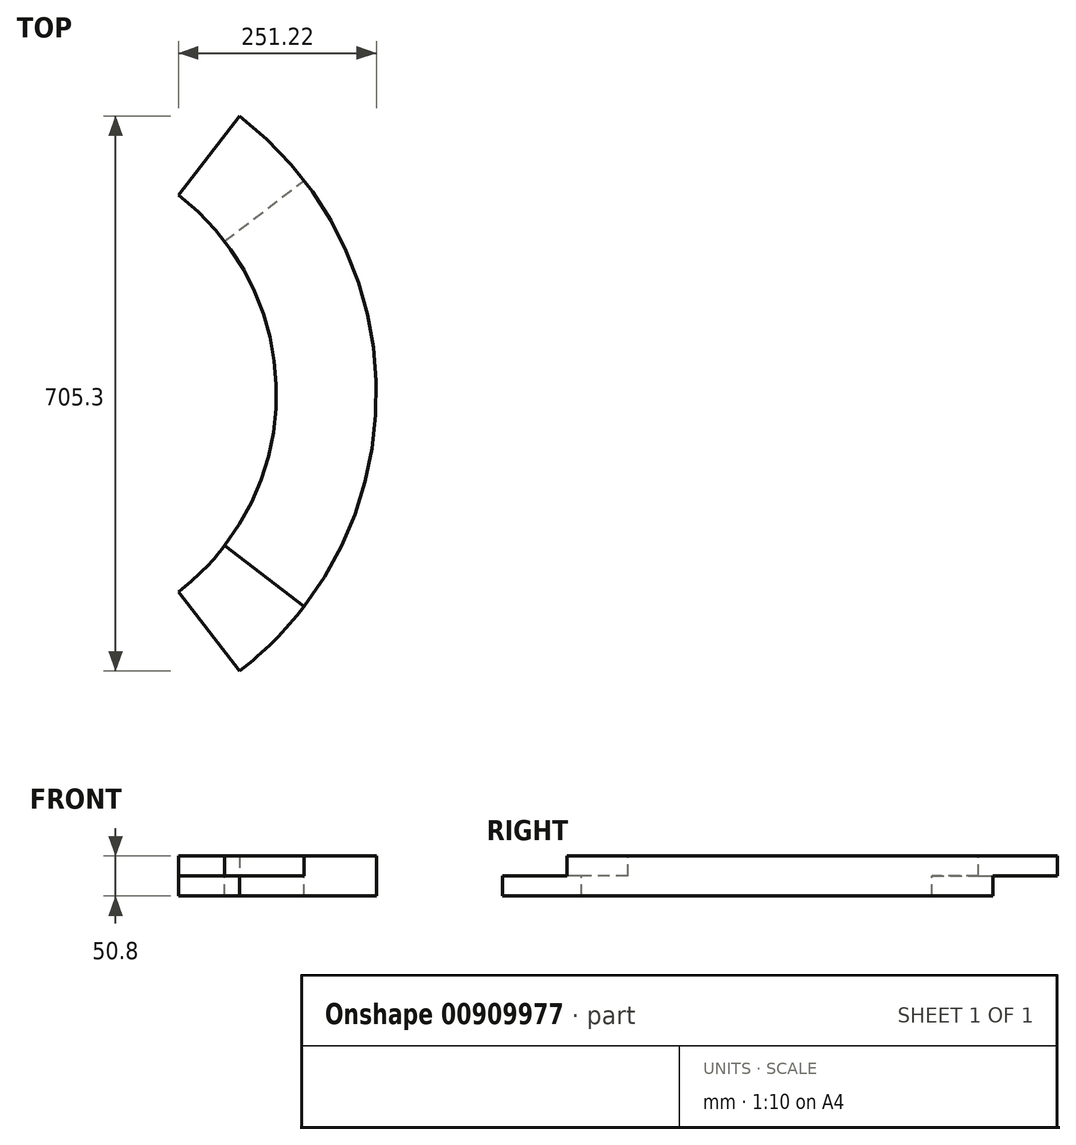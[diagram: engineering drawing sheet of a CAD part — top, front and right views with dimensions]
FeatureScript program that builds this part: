
annotation { "Feature Type Name" : "Feature", "Feature Type Description" : "" }
export const myFeature = defineFeature(function(context is Context, id is Id, definition is map)
    precondition{}
    {
        {
            var Q0;
            Q0=qCreatedBy(makeId("Front.planeOp"),FACE);
            var sketch = newSketch(context, id + "F0", { "sketchPlane" : qUnion([Q0])});
            skLineSegment(sketch, "E0.bottom", {"start": v(317.5, 0) * mm, "end": v(444.5, 0) * mm});
            skLineSegment(sketch, "E0.top", {"start": v(317.5, 25.4) * mm, "end": v(444.5, 25.4) * mm});
            skLineSegment(sketch, "E0.left", {"start": v(317.5, 0) * mm, "end": v(317.5, 25.4) * mm});
            skLineSegment(sketch, "E0.right", {"start": v(444.5, 0) * mm, "end": v(444.5, 25.4) * mm});
            skLineSegment(sketch, "E1", {"start": v(317.5, 25.4) * mm, "end": v(317.5, 50.8) * mm});
            skLineSegment(sketch, "E2", {"start": v(317.5, 50.8) * mm, "end": v(444.5, 50.8) * mm});
            skLineSegment(sketch, "E3", {"start": v(444.5, 50.8) * mm, "end": v(444.5, 25.4) * mm});
            skLineSegment(sketch, "E4", {"start": v(0, 0) * mm, "end": v(0, 51.24) * mm, "construction": true});
            skSolve(sketch);
        }
        {
            var Q0;
            Q0=makeQuery(id+"F0.imprint","IMPRINT",FACE,{"disambiguationData":[TD([[makeQuery(id+"F0.imprint","IMPRINT",EDGE,{"derivedFrom":sQuery(id+"F0.wireOp",EDGE,"E0.bottom")}),1.0]])]});
            var Q1;
            Q1=sQuery(id+"F0.wireOp",EDGE,"E4");
            revolve(context, id + "F1", {"surfaceOperationType" : NewSurfaceOperationType.NEW, "entities" : qUnion([Q0]), "axis" : qUnion([Q1]), "revolveType" : RevolveType.TWO_DIRECTIONS, "angle" : 37.5 * degree, "angleBack" : 307.5 * degree});
        }
        {
            var Q0;
            Q0=makeQuery(id+"F0.imprint","IMPRINT",FACE,{"disambiguationData":[TD([[makeQuery(id+"F0.imprint","IMPRINT",EDGE,{"derivedFrom":sQuery(id+"F0.wireOp",EDGE,"E0.top")}),1.0]])]});
            var Q1;
            Q1=sQuery(id+"F0.wireOp",EDGE,"E4");
            revolve(context, id + "F2", {"operationType" : NewBodyOperationType.ADD, "surfaceOperationType" : NewSurfaceOperationType.NEW, "entities" : qUnion([Q0]), "axis" : qUnion([Q1]), "revolveType" : RevolveType.TWO_DIRECTIONS, "angle" : 52.5 * degree, "angleBack" : 322.5 * degree});
        }
    });
